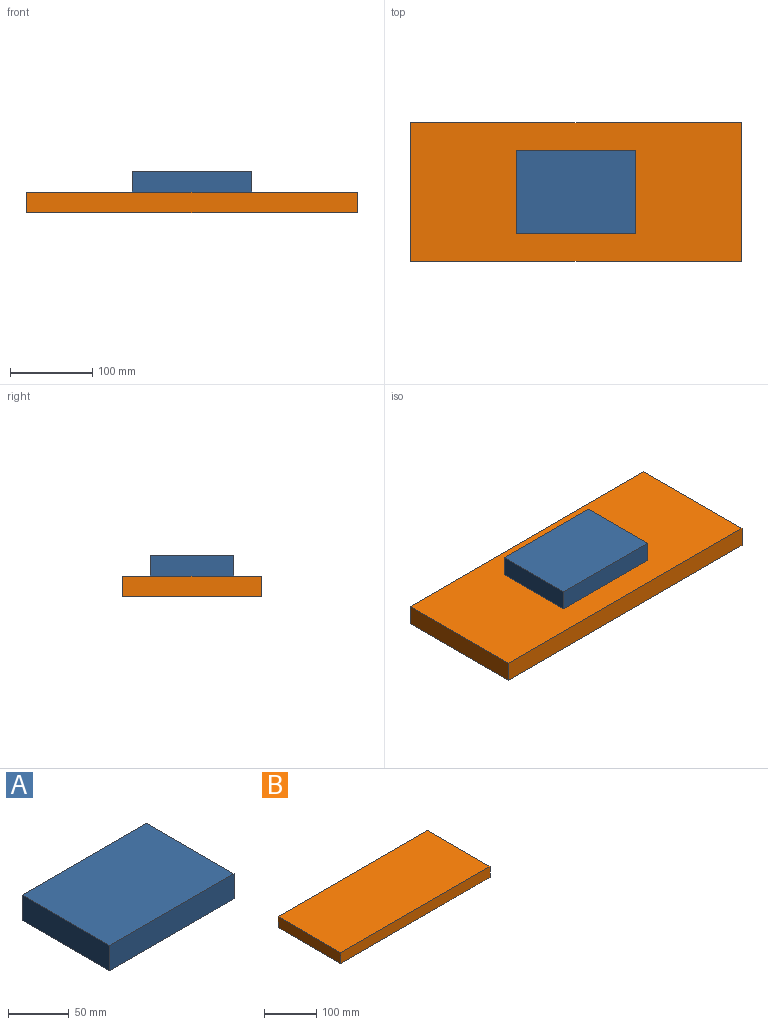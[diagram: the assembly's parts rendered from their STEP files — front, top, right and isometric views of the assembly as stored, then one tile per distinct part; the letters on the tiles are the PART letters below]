
ASSEMBLY  parts=2 mates=1
PART A: 6 faces, bbox 144.9x102.1x25.4 mm
  f0: plane 102.13x25.4mm, normal (-1,0,0), area 2594.1mm2, adj f1,f3,f4,f5
  f1: plane 144.95x25.4mm, normal (0,-1,0), area 3681.7mm2, adj f0,f2,f4,f5
  f2: plane 102.13x25.4mm, normal (1,0,0), area 2594.1mm2, adj f1,f3,f4,f5
  f3: plane 144.95x25.4mm, normal (0,1,0), area 3681.7mm2, adj f0,f2,f4,f5
  f4: plane 144.95x102.13mm, normal (0,0,1), area 14803.4mm2, adj f0,f1,f2,f3
  f5: plane 144.95x102.13mm, normal (0,0,-1), area 14803.4mm2, adj f0,f1,f2,f3
PART B: 6 faces, bbox 402.6x169x25.4 mm
  f0: plane 169.02x25.4mm, normal (-1,0,0), area 4293.2mm2, adj f1,f3,f4,f5
  f1: plane 402.65x25.4mm, normal (0,-1,0), area 10227.2mm2, adj f0,f2,f4,f5
  f2: plane 169.02x25.4mm, normal (1,0,0), area 4293.2mm2, adj f1,f3,f4,f5
  f3: plane 402.65x25.4mm, normal (0,1,0), area 10227.2mm2, adj f0,f2,f4,f5
  f4: plane 402.65x169.02mm, normal (0,0,1), area 68056.8mm2, adj f0,f1,f2,f3
  f5: plane 402.65x169.02mm, normal (0,0,-1), area 68056.8mm2, adj f0,f1,f2,f3
PLACE A t=(272.5,144.57,-211.25)mm
PLACE B t=(190.04,173.24,-236.65)mm
MATE revolute B.f4 <-> A.f5  axis (0,0,1) through (215.27,105.75,-211.25)mm
